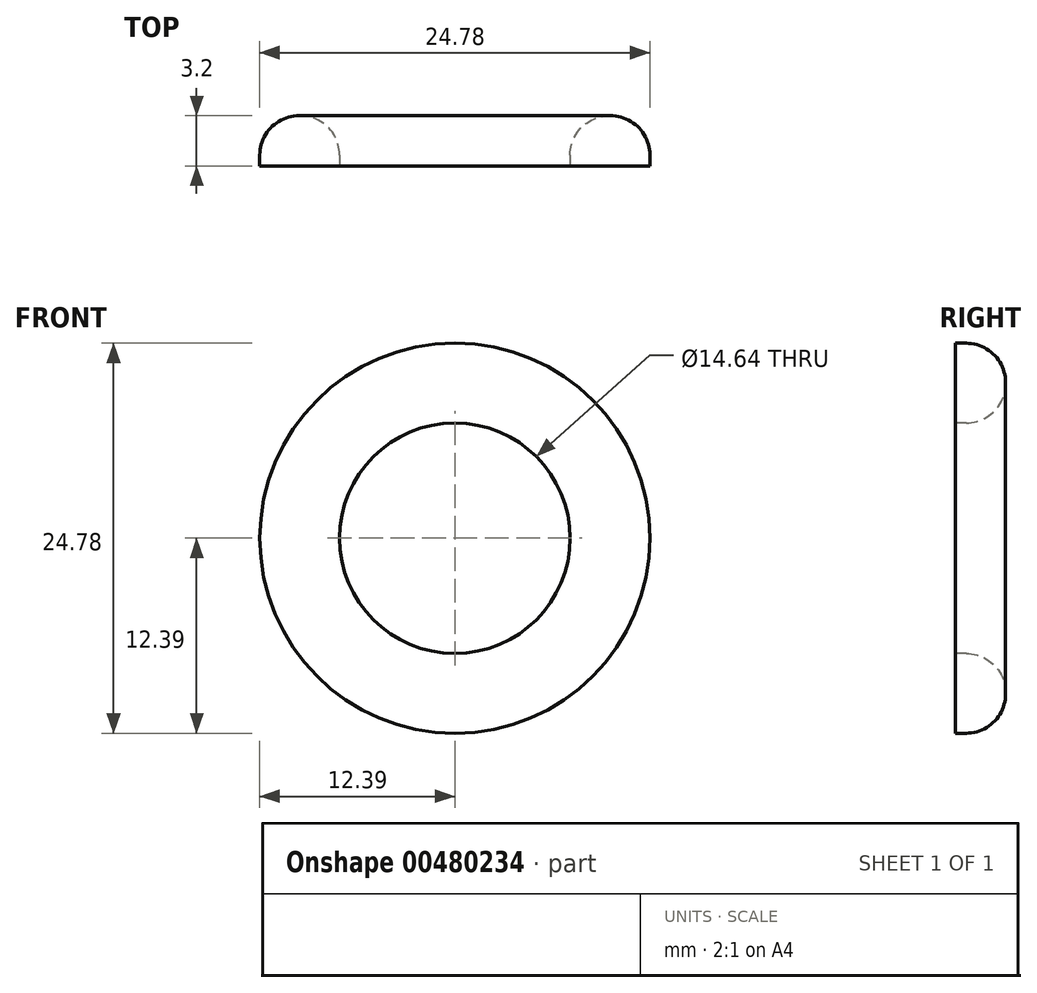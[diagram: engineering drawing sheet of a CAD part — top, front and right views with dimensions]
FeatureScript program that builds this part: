
annotation { "Feature Type Name" : "Feature", "Feature Type Description" : "" }
export const myFeature = defineFeature(function(context is Context, id is Id, definition is map)
    precondition{}
    {
        {
            var Q0;
            Q0=qCreatedBy(makeId("Front.planeOp"),FACE);
            var sketch = newSketch(context, id + "F0", { "sketchPlane" : qUnion([Q0])});
            skCircle(sketch, "E0", {"center": v(0, 0) * mm, "radius": 12.39 * mm});
            skCircle(sketch, "E1", {"center": v(0, 0) * mm, "radius": 7.32 * mm});
            skSolve(sketch);
        }
        {
            var Q0;
            Q0 = qSketchRegion(id + "F0", true);
            extrude(context, id + "F1", {"entities" : qUnion([Q0]), "oppositeDirection" : true, "depth" : 3.2 * mm});
        }
        {
            var Q0;
            Q0=makeQuery(id+"F1.opExtrude","CAP_FACE",FACE,{"disambiguationData":[OSD([sQuery(id+"F0.wireOp",EDGE,"E0"),sQuery(id+"F0.wireOp",EDGE,"E1")])],"isStart":false});
            fillet(context, id + "F2", {"entities" : qUnion([Q0]), "radius" : 2.5 * mm, "tangentPropagation" : true, "allowEdgeOverflow" : false});
        }
    });
